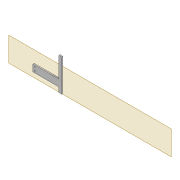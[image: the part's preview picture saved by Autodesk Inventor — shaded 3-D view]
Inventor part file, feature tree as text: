
AUTODESK INVENTOR PART (.ipt)
format: ipt  version: 2022 (Build 260153000, 153)  size: 599,040 bytes
history: native  units: mm
features: projected_geometry x9, extrude x8, sketch x8, fillet x2, shell x1, plane x1, chamfer x1
ambient origin geometry x8: Origin, YZ Plane, XZ Plane, XY Plane, X Axis, Y Axis, Z Axis, Center Point
bodies: Solid1 (feature_tree)
feature tree (30):
  extrude  "Extrusion1"  Depth=2.0mm
  shell  "Shell1"  Thickness=2.0mm
  extrude  "Extrusion8"  Depth=2.0mm
  extrude  "Extrusion3"  Depth=10.0mm TaperAngle=0.0deg
  extrude  "Extrusion4"  Depth=2.0mm
  fillet  "Fillet1"  Radius=5.0mm
  sketch  "Sketch10"  dims[d22=2.0mm d23=0.0mm d31=2.0mm d32=5.0mm]
  extrude  "Extrusion5"  Depth=2.0mm
  plane  "Work Plane2"
  extrude  "Extrusion9"  Depth=2.0mm
  fillet  "Fillet2"  Radius=2.5mm
  extrude  "Extrusion10"  Depth=2.0mm
  chamfer  "Chamfer1"  Distance=2.0mm
  extrude  "Extrusion13"  Depth=12.0mm
  sketch  "Sketch31"  dims[d37=5.0mm d38=2.0mm d40=2.5mm]
  sketch  "Sketch35"  dims[d66=3.0mm d67=12.0mm d68=5.0mm d69=45.0mm d70=12.0mm d71=3.05mm d72=10.0mm d73=0.0mm d74=2.0mm d75=100.0mm d76=20.0mm d77=0.5mm d78=10.0mm d79=0.0mm d109=45.0deg d129=3.0mm d130=2.0mm d131=45.0deg d132=1.0mm d133=1.0mm d134=10.0mm d135=0.0mm d136=1.0mm d137=1.0mm d138=1.0mm d139=1.0mm d140=20.0mm]
  sketch  "Sketch3"  dims[d0=2.0mm d1=0.0mm d2=4.0mm d7=2.0mm]
  sketch  "Sketch8"  dims[d8=2.0mm d9=5.9mm]
  sketch  "Sketch9"  dims[d13=10.0mm d14=0.0mm d16=10.0mm d17=0.0mm]
  projected_geometry  "Projected Loop4"
  projected_geometry  "Projected Loop10"
  sketch  "Sketch24"  dims[d34=2.0mm d35=2.5mm]
  projected_geometry  "Projected Loop11"
  projected_geometry  "Projected Loop12"
  projected_geometry  "Projected Loop13"
  projected_geometry  "Projected Loop14"
  sketch  "Sketch32"  dims[d62=80.0mm d63=6.0mm d64=2.0mm d65=0.0mm]
  projected_geometry  "Project Cut Edges3"
  projected_geometry  "Project Cut Edges5"
  projected_geometry  "Project Cut Edges7"
